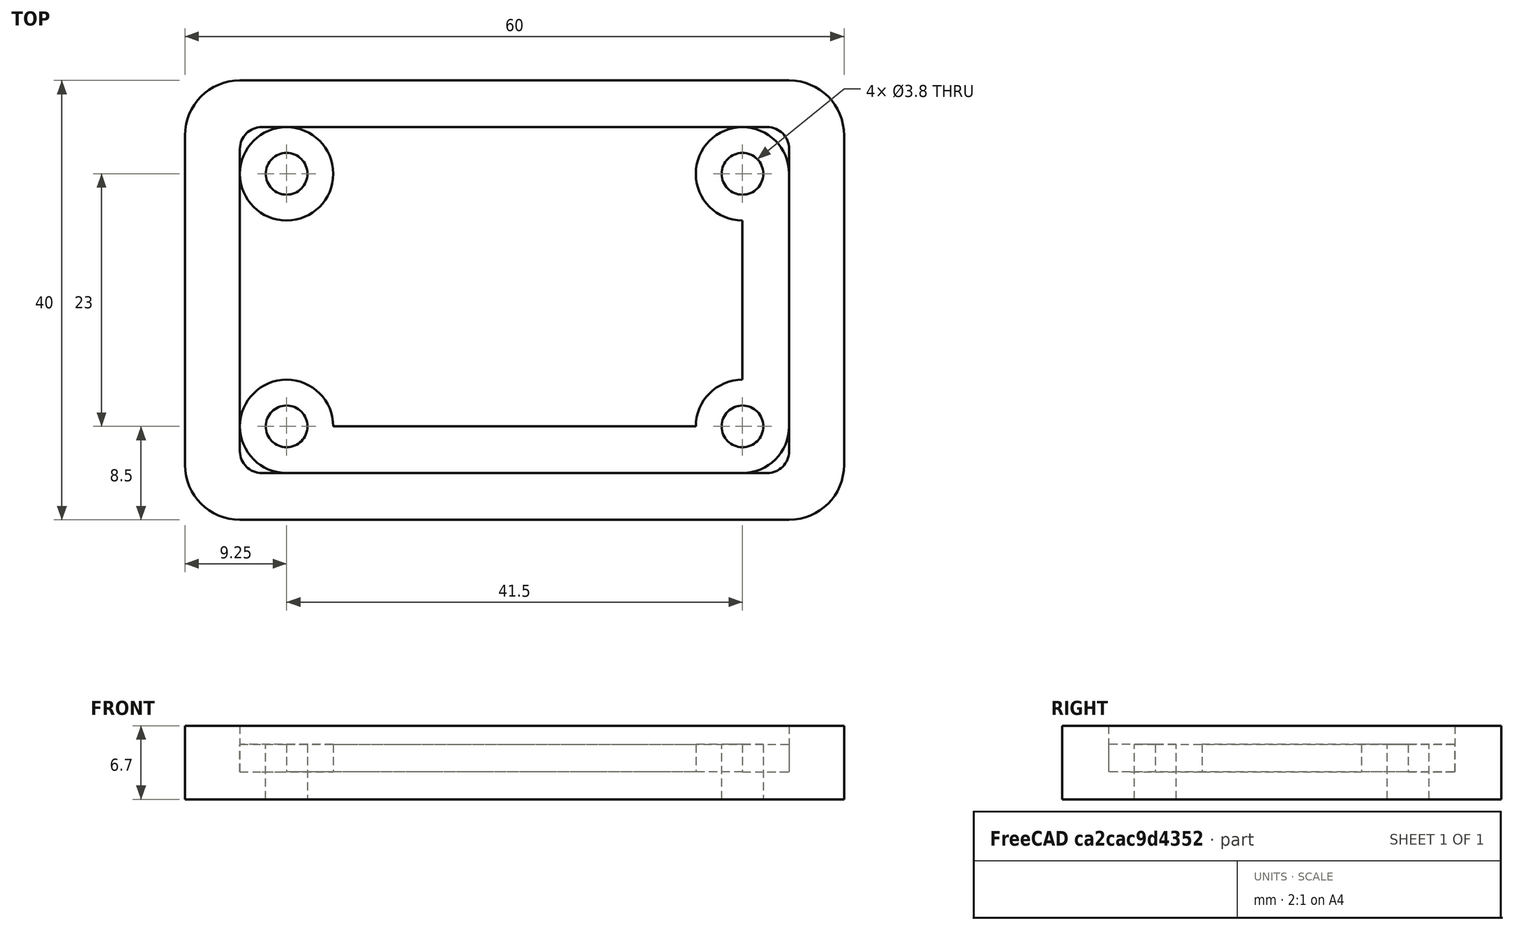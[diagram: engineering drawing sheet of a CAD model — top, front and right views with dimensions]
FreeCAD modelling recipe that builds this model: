
FCSTD DOCUMENT  (FreeCAD 0.21R33694 (Git))
Label: backing_plate
License: All rights reserved
LicenseURL: http://en.wikipedia.org/wiki/All_rights_reserved
objects: Sketcher::SketchObject×4, PartDesign::Plane×3, PartDesign::Pad×2, PartDesign::Pocket×2, PartDesign::Body×1
note: 16 computed .brp shape members not serialized (recipe doc carries the construction recipe); baked Part::Feature solids carry a one-line shape summary decoded from their .brp

FEATURE [PartDesign::Plane] DatumPlane  label="PCB Bottom"
  AttachmentOffset = pos=(0,0,5) rot=(0,0,1;0rad)
  Length = 60
  MapMode = 5
  Placement = pos=(0,0,5) rot=(0,0,1;0rad)
  ResizeMode = 0
  Support = -> [XY_Plane]
  Width = 60
FEATURE [PartDesign::Plane] DatumPlane001  label="PCB Top"
  AttachmentOffset = pos=(0,0,1.7) rot=(0,0,1;0rad)
  Length = 60
  MapMode = 5
  Placement = pos=(0,0,6.7) rot=(0,0,1;0rad)
  ResizeMode = 0
  Support = -> [DatumPlane]
  Width = 60
FEATURE [Sketcher::SketchObject] Sketch  label="PCB Outline"
  FullyConstrained = true
  MapMode = 5
  Placement = pos=(0,0,6.7) rot=(0,0,1;0rad)
  Support = -> [DatumPlane001]
  sketch-geometry (8):
    g0: LineSegment StartX=-23 StartY=15.75 StartZ=0 EndX=23 EndY=15.75 EndZ=0
    g1: LineSegment StartX=25 StartY=13.75 StartZ=0 EndX=25 EndY=-13.75 EndZ=0
    g2: LineSegment StartX=23 StartY=-15.75 StartZ=0 EndX=-23 EndY=-15.75 EndZ=0
    g3: LineSegment StartX=-25 StartY=-13.75 StartZ=0 EndX=-25 EndY=13.75 EndZ=0
    g4: ArcOfCircle CenterX=-23 CenterY=13.75 CenterZ=0 NormalX=0 NormalY=0 NormalZ=1 AngleXU=0 Radius=2 StartAngle=1.5708 EndAngle=3.14159
    g5: ArcOfCircle CenterX=-23 CenterY=-13.75 CenterZ=0 NormalX=0 NormalY=0 NormalZ=1 AngleXU=0 Radius=2 StartAngle=3.14159 EndAngle=4.71239
    g6: ArcOfCircle CenterX=23 CenterY=-13.75 CenterZ=0 NormalX=0 NormalY=0 NormalZ=1 AngleXU=0 Radius=2 StartAngle=4.71239 EndAngle=6.28319
    g7: ArcOfCircle CenterX=23 CenterY=13.75 CenterZ=0 NormalX=0 NormalY=0 NormalZ=1 AngleXU=0 Radius=2 StartAngle=0 EndAngle=1.5708
  constraints (18):
    c: Horizontal(g0)
    c: Horizontal(g2)
    c: Vertical(g1)
    c: Vertical(g3)
    c: Tangent(g0,g4) = 1.5708
    c: Tangent(g3,g4) = 1.5708
    c: Tangent(g3,g5) = 1.5708
    c: Tangent(g2,g5) = 1.5708
    c: Tangent(g2,g6) = 1.5708
    c: Tangent(g1,g6) = 1.5708
    c: Tangent(g1,g7) = 1.5708
    c: Tangent(g0,g7) = 1.5708
    c: Equal(g6,g5)
    c: Symmetric(g4,g7,g-2)
    c: Symmetric(g7,g6,g-1)
    c: DistanceX(g3,g1) = 50
    c: DistanceY(g2,g0) = 31.5
    c: Radius(g5) = 2
FEATURE [Sketcher::SketchObject] Sketch001  label="Plate Outline"
  FullyConstrained = true
  MapMode = 5
  Support = -> [XY_Plane]
  sketch-geometry (8):
    g0: LineSegment StartX=-25 StartY=20 StartZ=0 EndX=25 EndY=20 EndZ=0
    g1: LineSegment StartX=30 StartY=15 StartZ=0 EndX=30 EndY=-15 EndZ=0
    g2: LineSegment StartX=25 StartY=-20 StartZ=0 EndX=-25 EndY=-20 EndZ=0
    g3: LineSegment StartX=-30 StartY=-15 StartZ=0 EndX=-30 EndY=15 EndZ=0
    g4: ArcOfCircle CenterX=-25 CenterY=15 CenterZ=0 NormalX=0 NormalY=0 NormalZ=1 AngleXU=0 Radius=5 StartAngle=1.5708 EndAngle=3.14159
    g5: ArcOfCircle CenterX=25 CenterY=15 CenterZ=0 NormalX=0 NormalY=0 NormalZ=1 AngleXU=0 Radius=5 StartAngle=1.066e-13 EndAngle=1.5708
    g6: ArcOfCircle CenterX=25 CenterY=-15 CenterZ=0 NormalX=0 NormalY=0 NormalZ=1 AngleXU=0 Radius=5 StartAngle=4.71239 EndAngle=6.28319
    g7: ArcOfCircle CenterX=-25 CenterY=-15 CenterZ=0 NormalX=0 NormalY=0 NormalZ=1 AngleXU=0 Radius=5 StartAngle=3.14159 EndAngle=4.71239
  constraints (18):
    c: Horizontal(g0)
    c: Horizontal(g2)
    c: Vertical(g1)
    c: Vertical(g3)
    c: Tangent(g0,g4) = 1.5708
    c: Tangent(g3,g4) = 1.5708
    c: Tangent(g0,g5) = 1.5708
    c: Tangent(g1,g5) = 1.5708
    c: Tangent(g1,g6) = 1.5708
    c: Tangent(g2,g6) = 1.5708
    c: Tangent(g2,g7) = 1.5708
    c: Tangent(g3,g7) = 1.5708
    c: Equal(g6,g7)
    c: Radius(g7) = 5
    c: Symmetric(g4,g5,g-2)
    c: Symmetric(g5,g6,g-1)
    c: DistanceX(g3,g1) = 60
    c: DistanceY(g2,g0) = 40
FEATURE [PartDesign::Pad] Pad  label="Plate"
  Direction = (0,0,1)
  Length = 10
  Length2 = 10
  Profile = -> Sketch001
  ReferenceAxis = -> Sketch001 [N_Axis]
  Type = 3
  UpToFace = -> DatumPlane001 [Plane]
FEATURE [PartDesign::Plane] DatumPlane002  label="PCB Bottom Clear"
  AttachmentOffset = pos=(0,0,-2.5) rot=(0,0,1;0rad)
  Length = 60
  MapMode = 5
  Placement = pos=(0,0,2.5) rot=(0,0,1;0rad)
  ResizeMode = 0
  Support = -> [DatumPlane]
  Width = 60
FEATURE [PartDesign::Pocket] Pocket  label="PCB Cutout"
  BaseFeature = -> Pad
  Direction = (0,0,-1)
  Length = 0
  Length2 = 5
  Profile = -> Sketch
  ReferenceAxis = -> Sketch [N_Axis]
  Type = 3
  UpToFace = -> DatumPlane002 [Plane]
FEATURE [Sketcher::SketchObject] Sketch002  label="PCB Mounting Holes"
  FullyConstrained = true
  MapMode = 5
  Placement = pos=(0,0,6.7) rot=(0,0,1;0rad)
  Support = -> [DatumPlane001]
  sketch-geometry (8):
    g0: Circle CenterX=-20.75 CenterY=11.5 CenterZ=0 NormalX=0 NormalY=0 NormalZ=1 AngleXU=0 Radius=1.9
    g1: Circle CenterX=-20.75 CenterY=-11.5 CenterZ=0 NormalX=0 NormalY=0 NormalZ=1 AngleXU=0 Radius=1.9
    g2: Circle CenterX=20.75 CenterY=11.5 CenterZ=0 NormalX=0 NormalY=0 NormalZ=1 AngleXU=0 Radius=1.9
    g3: Circle CenterX=20.75 CenterY=-11.5 CenterZ=0 NormalX=0 NormalY=0 NormalZ=1 AngleXU=0 Radius=1.9
    g4: LineSegment StartX=-20.75 StartY=11.5 StartZ=0 EndX=20.75 EndY=11.5 EndZ=0
    g5: LineSegment StartX=20.75 StartY=11.5 StartZ=0 EndX=20.75 EndY=-11.5 EndZ=0
    g6: LineSegment StartX=20.75 StartY=-11.5 StartZ=0 EndX=-20.75 EndY=-11.5 EndZ=0
    g7: LineSegment StartX=-20.75 StartY=-11.5 StartZ=0 EndX=-20.75 EndY=11.5 EndZ=0
  constraints (18):
    c: Equal(g2,g0)
    c: Equal(g0,g1)
    c: Equal(g1,g3)
    c: Coincident(g4,g5)
    c: Coincident(g5,g6)
    c: Coincident(g6,g7)
    c: Coincident(g7,g4)
    c: Horizontal(g6)
    c: Vertical(g7)
    c: Coincident(g0,g4)
    c: Coincident(g1,g6)
    c: Coincident(g2,g4)
    c: Coincident(g3,g5)
    c: Symmetric(g0,g2,g-2)
    c: Symmetric(g2,g3,g-1)
    c: DistanceY(g5,g5) = 23
    c: DistanceX(g4,g4) = 41.5
    c: Diameter(g1) = 3.8
FEATURE [Sketcher::SketchObject] Sketch003  label="PCB Mount Supports Outline"
  FullyConstrained = true
  MapMode = 5
  Placement = pos=(0,0,5) rot=(0,0,1;0rad)
  Support = -> [DatumPlane]
  sketch-geometry (17):
    g0: Circle CenterX=-20.75 CenterY=11.5 CenterZ=0 NormalX=0 NormalY=0 NormalZ=1 AngleXU=0 Radius=4.25
    g1: Circle CenterX=20.75 CenterY=11.5 CenterZ=0 NormalX=0 NormalY=0 NormalZ=1 AngleXU=0 Radius=4.25
    g2: Circle CenterX=20.75 CenterY=-11.5 CenterZ=0 NormalX=0 NormalY=0 NormalZ=1 AngleXU=0 Radius=4.25
    g3: Circle CenterX=-20.75 CenterY=-11.5 CenterZ=0 NormalX=0 NormalY=0 NormalZ=1 AngleXU=0 Radius=4.25
    g4: LineSegment StartX=-20.75 StartY=11.5 StartZ=0 EndX=20.75 EndY=11.5 EndZ=0
    g5: LineSegment StartX=20.75 StartY=11.5 StartZ=0 EndX=20.75 EndY=-11.5 EndZ=0
    g6: LineSegment StartX=20.75 StartY=-11.5 StartZ=0 EndX=-20.75 EndY=-11.5 EndZ=0
    g7: LineSegment StartX=-20.75 StartY=-11.5 StartZ=0 EndX=-20.75 EndY=11.5 EndZ=0
    g8: LineSegment StartX=-20.75 StartY=-15.75 StartZ=0 EndX=20.75 EndY=-15.75 EndZ=0
    g9: LineSegment StartX=-16.5 StartY=-11.5 StartZ=0 EndX=16.5 EndY=-11.5 EndZ=0
    g10: ArcOfCircle CenterX=20.75 CenterY=-11.5 CenterZ=0 NormalX=0 NormalY=0 NormalZ=1 AngleXU=0 Radius=4.25 StartAngle=4.71239 EndAngle=6.28319
    g11: ArcOfCircle CenterX=-20.75 CenterY=-11.5 CenterZ=0 NormalX=0 NormalY=0 NormalZ=1 AngleXU=0 Radius=4.25 StartAngle=1e-16 EndAngle=4.71238
    g12: ArcOfCircle CenterX=20.75 CenterY=-11.5 CenterZ=0 NormalX=0 NormalY=0 NormalZ=1 AngleXU=0 Radius=4.25 StartAngle=1.5708 EndAngle=3.14159
    g13: ArcOfCircle CenterX=20.75 CenterY=11.5 CenterZ=0 NormalX=0 NormalY=0 NormalZ=1 AngleXU=0 Radius=4.25 StartAngle=6.28319 EndAngle=10.9956
    g14: LineSegment StartX=20.75 StartY=7.25 StartZ=0 EndX=20.75 EndY=-7.25 EndZ=0
    g15: LineSegment StartX=25 StartY=-11.5 StartZ=0 EndX=25 EndY=11.5 EndZ=0
    g16: Circle CenterX=-20.75 CenterY=11.5 CenterZ=0 NormalX=0 NormalY=0 NormalZ=1 AngleXU=0 Radius=4.25
  constraints (43):
    c: Coincident(g4,g5)
    c: Coincident(g5,g6)
    c: Coincident(g6,g7)
    c: Coincident(g7,g4)
    c: Horizontal(g6)
    c: Vertical(g7)
    c: Coincident(g4,g0)
    c: Coincident(g5,g2)
    c: Coincident(g1,g4)
    c: Coincident(g3,g6)
    c: Equal(g1,g2)
    c: Equal(g2,g3)
    c: Equal(g3,g0)
    c: Diameter(g3) = 8.5
    c: Symmetric(g0,g1,g-2)
    c: Symmetric(g1,g2,g-1)
    c: DistanceX(g4,g4) = 41.5
    c: DistanceY(g5,g5) = 23
    c: Horizontal(g8)
    c: PointOnObject(g9,g2)
    c: Horizontal(g9)
    c: PointOnObject(g13,g1)
    c: Coincident(g10,g2)
    c: Coincident(g10,g8)
    c: Coincident(g11,g3)
    c: Coincident(g11,g8)
    c: Coincident(g12,g10)
    c: Coincident(g12,g9)
    c: Tangent(g8,g2) = -1.5708
    c: PointOnObject(g13,g5)
    c: PointOnObject(g9,g6)
    c: Coincident(g13,g1)
    c: Coincident(g14,g13)
    c: Coincident(g14,g12)
    c: Vertical(g14)
    c: Coincident(g15,g10)
    c: Coincident(g15,g13)
    c: Vertical(g15)
    c: Tangent(g15,g1)
    c: Coincident(g16,g0)
    c: Equal(g16,g0)
    c: Coincident(g11,g9)
    c: Equal(g11,g3)
FEATURE [PartDesign::Pad] Pad001  label="PCB Mount Supports"
  BaseFeature = -> Pocket
  Direction = (0,0,1)
  Length = 10
  Length2 = 10
  Profile = -> Sketch003
  ReferenceAxis = -> Sketch003 [N_Axis]
  Type = 3
  UpToFace = -> DatumPlane002
FEATURE [PartDesign::Pocket] Pocket001  label="PCB Mounting Holes Cutout"
  BaseFeature = -> Pad001
  Direction = (0,0,-1)
  Length = 0
  Length2 = 5
  Profile = -> Sketch002
  ReferenceAxis = -> Sketch002 [N_Axis]
  Type = 3
  UpToFace = -> XY_Plane
FEATURE [PartDesign::Body] Body
  Group = -> [DatumPlane,DatumPlane002,DatumPlane001,Sketch001,Pad,Sketch,Pocket,Sketch003,Pad001,Sketch002,Pocket001]
  Origin = -> Origin
  Tip = -> Pocket001
